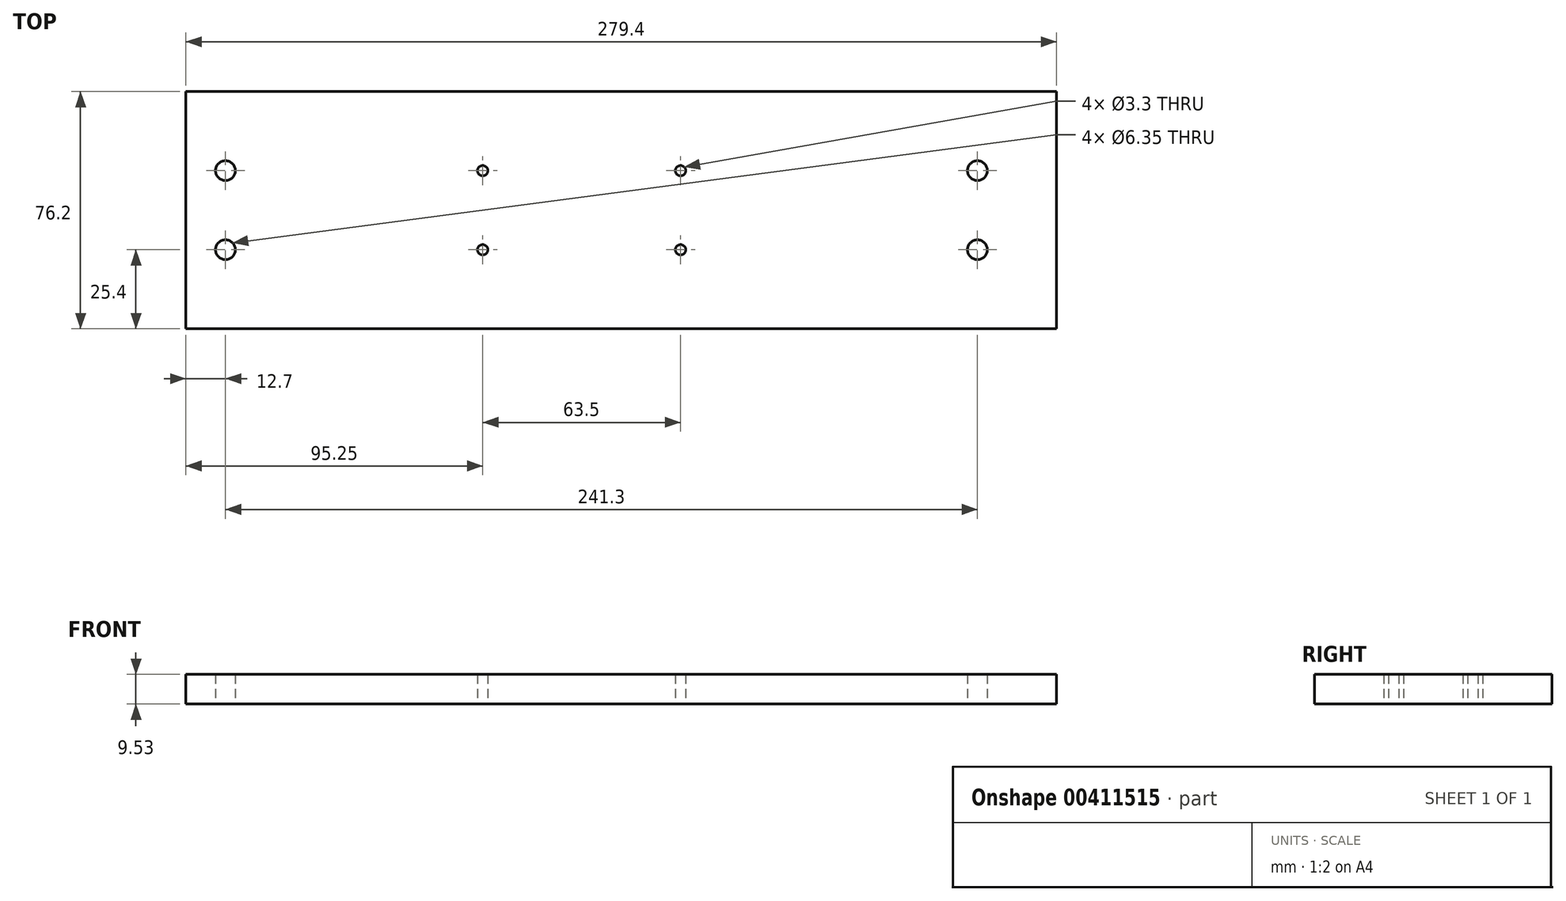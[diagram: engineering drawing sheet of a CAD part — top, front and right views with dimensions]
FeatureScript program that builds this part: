
annotation { "Feature Type Name" : "Feature", "Feature Type Description" : "" }
export const myFeature = defineFeature(function(context is Context, id is Id, definition is map)
    precondition{}
    {
        {
            var Q0;
            Q0=qCreatedBy(makeId("Top.planeOp"),FACE);
            var sketch = newSketch(context, id + "F0", { "sketchPlane" : qUnion([Q0])});
            skLineSegment(sketch, "E0.bottom", {"start": v(0, 0) * mm, "end": v(279.4, 0) * mm});
            skLineSegment(sketch, "E0.top", {"start": v(0, 76.2) * mm, "end": v(279.4, 76.2) * mm});
            skLineSegment(sketch, "E0.left", {"start": v(0, 0) * mm, "end": v(0, 76.2) * mm});
            skLineSegment(sketch, "E0.right", {"start": v(279.4, 0) * mm, "end": v(279.4, 76.2) * mm});
            skCircle(sketch, "E1", {"center": v(12.7, 50.8) * mm, "radius": 3.18 * mm});
            skCircle(sketch, "E2", {"center": v(12.7, 25.4) * mm, "radius": 3.18 * mm});
            skCircle(sketch, "E3", {"center": v(254, 50.8) * mm, "radius": 3.18 * mm});
            skCircle(sketch, "E4", {"center": v(254, 25.4) * mm, "radius": 3.18 * mm});
            skCircle(sketch, "E5", {"center": v(95.25, 50.8) * mm, "radius": 1.65 * mm});
            skCircle(sketch, "E6", {"center": v(158.75, 50.8) * mm, "radius": 1.65 * mm});
            skCircle(sketch, "E7", {"center": v(158.75, 25.4) * mm, "radius": 1.65 * mm});
            skCircle(sketch, "E8", {"center": v(95.25, 25.4) * mm, "radius": 1.65 * mm});
            skSolve(sketch);
        }
        {
            var Q0;
            Q0=makeQuery(id+"F0.imprint","IMPRINT",FACE,{"disambiguationData":[TD([[makeQuery(id+"F0.imprint","IMPRINT",EDGE,{"derivedFrom":sQuery(id+"F0.wireOp",EDGE,"E0.bottom")}),1.0]])]});
            extrude(context, id + "F1", {"entities" : qUnion([Q0]), "depth" : 9.52 * mm});
        }
    });
